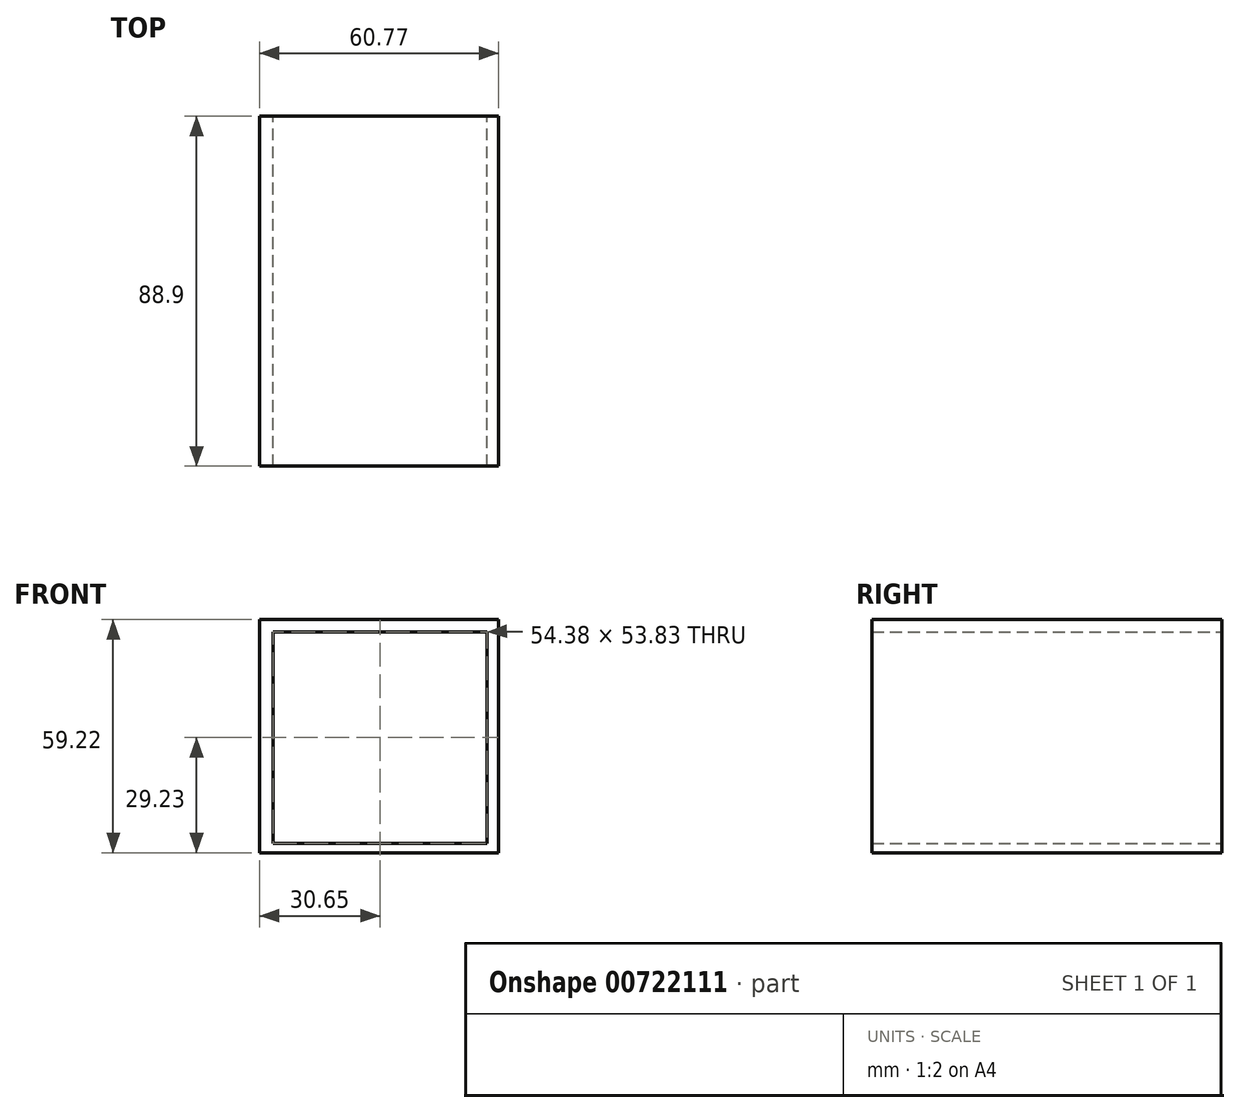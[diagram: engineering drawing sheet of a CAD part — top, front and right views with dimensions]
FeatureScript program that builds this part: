
annotation { "Feature Type Name" : "Feature", "Feature Type Description" : "" }
export const myFeature = defineFeature(function(context is Context, id is Id, definition is map)
    precondition{}
    {
        {
            var Q0;
            Q0=qCreatedBy(makeId("Front.planeOp"),FACE);
            var sketch = newSketch(context, id + "F0", { "sketchPlane" : qUnion([Q0])});
            skLineSegment(sketch, "E0.bottom", {"start": v(-66.23, 65.11) * mm, "end": v(-5.46, 65.11) * mm});
            skLineSegment(sketch, "E0.top", {"start": v(-66.23, 5.9) * mm, "end": v(-5.46, 5.9) * mm});
            skLineSegment(sketch, "E0.left", {"start": v(-66.23, 65.11) * mm, "end": v(-66.23, 5.9) * mm});
            skLineSegment(sketch, "E0.right", {"start": v(-5.46, 65.11) * mm, "end": v(-5.46, 5.9) * mm});
            skLineSegment(sketch, "E1.bottom", {"start": v(-62.77, 62.04) * mm, "end": v(-8.39, 62.04) * mm});
            skLineSegment(sketch, "E1.top", {"start": v(-62.77, 8.2) * mm, "end": v(-8.39, 8.2) * mm});
            skLineSegment(sketch, "E1.left", {"start": v(-62.77, 62.04) * mm, "end": v(-62.77, 8.2) * mm});
            skLineSegment(sketch, "E1.right", {"start": v(-8.39, 62.04) * mm, "end": v(-8.39, 8.2) * mm});
            skLineSegment(sketch, "E2", {"start": v(-61.11, 62.04) * mm, "end": v(-61.11, 8.2) * mm});
            skSolve(sketch);
        }
        {
            var Q0;
            Q0 = qSketchRegion(id + "F0", true);
            extrude(context, id + "F1", {"entities" : qUnion([Q0]), "depth" : 88.9 * mm, "offsetDistance" : 25.4 * mm});
        }
    });
